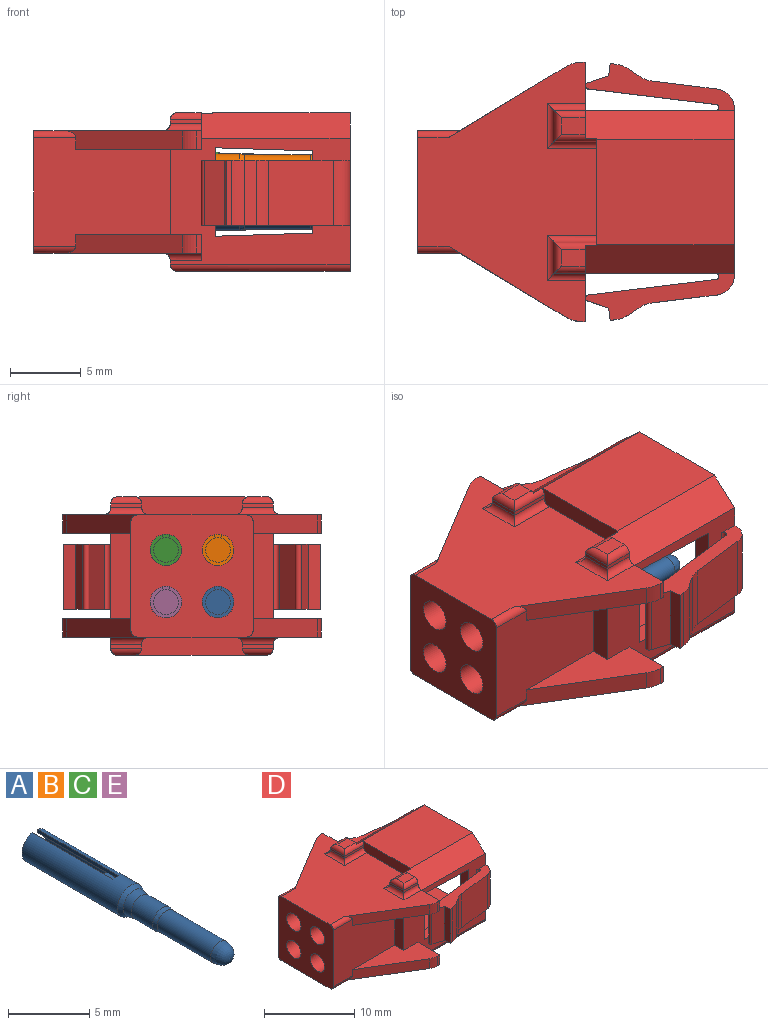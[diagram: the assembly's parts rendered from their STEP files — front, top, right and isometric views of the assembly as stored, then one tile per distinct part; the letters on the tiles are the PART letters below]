
ASSEMBLY  parts=5 mates=4
PART A: 14 faces, bbox 2.2x17x2.2 mm
  f0: cylinder r=0.88mm len=6mm, axis (0,-1,0), area 29.9mm2, adj f8,f9,f10,f12
  f1: cylinder r=0.78mm len=4.65mm, axis (0,-1,0), area 22.6mm2, adj f2,f5
  f2: bspline ~1.71x1.71mm, area 1.6mm2, adj f1,f3
  f3: bspline ~1.86x1.71mm, area 9.9mm2, adj f2,f4
  f4: bspline ~1.86x1.86mm, area 3.5mm2, adj f3,f6
  f5: revolved ~1.55x1.55mm, area 4.4mm2, adj f1
  f6: cone r=0.93mm half-angle=32deg, axis (0,1,0), area 2.4mm2, adj f4,f7
  f7: cylinder r=1.12mm len=8.29mm, axis (0,-1,0), area 55mm2, adj f6,f8,f10,f12,f13
  f8: plane 2.25x2.22mm, normal (0,1,0), area 1.4mm2, adj f0,f7,f10,f12
  f9: plane 1.75x1.75mm, normal (0,1,0), area 2.4mm2, adj f0,f11
  f10: plane 7x0.26mm, normal (-1,0,0), area 1.8mm2, adj f0,f7,f8,f11,f13
  f11: cylinder r=0.88mm len=1mm, axis (0,1,0), area 0.5mm2, adj f9,f10,f12,f13
  f12: plane 7x0.26mm, normal (1,0,0), area 1.8mm2, adj f0,f7,f8,f11,f13
  f13: plane 0.5x0.29mm, normal (0,1,0), area 0.1mm2, adj f7,f10,f11,f12
PART B: same geometry as A
PART C: same geometry as A
PART D: 128 faces, bbox 22.3x18.3x11.2 mm
  f0: plane 2.19x0.28mm, normal (0,1,0), area 0.6mm2, adj f16,f40,f83,f86
  f1: plane 2.19x0.28mm, normal (0,-1,0), area 0.6mm2, adj f11,f49,f88,f91
  f2: plane 11.48x11.2mm, normal (1,0,0), area 43.5mm2, adj f4,f6,f7,f8,f9,f22,f27,f28
  f3: plane 1.69x1.19mm, normal (0,0,1), area 2mm2, adj f49,f91,f92,f93
  f4: plane 9.7x7.44mm, normal (0,0,1), area 72.1mm2, adj f2,f5,f98,f99
  f5: plane 7.59x1.28mm, normal (-1,0,0), area 9.1mm2, adj f4,f24,f60,f61,f82,f85,f90,f93
  f6: plane 13.2x8.88mm, normal (0,1,0), area 60.8mm2, adj f2,f10,f13,f25,f31,f40,f41,f55
  f7: plane 12.7x8.88mm, normal (0,-1,0), area 59.7mm2, adj f2,f14,f15,f31,f45,f49,f50,f51
  f8: plane 9.53x8.2mm, normal (0,-1,0), area 36.5mm2, adj f2,f27,f28,f31,f68,f69,f70
  f9: plane 9.53x8.2mm, normal (0,1,0), area 36.5mm2, adj f2,f27,f30,f31,f65,f66,f67
  f10: plane 2.19x0.28mm, normal (-1,0,0), area 0.6mm2, adj f6,f62,f73,f75
  f11: plane 2.19x0.28mm, normal (-1,0,0), area 0.6mm2, adj f1,f61,f89,f92
  f12: plane 9.64x7.64mm, normal (0,1,0), area 62.8mm2, adj f13,f26,f41,f44,f56,f57,f95,f96
  f13: plane 6.01x1.42mm, normal (-1,0,0), area 8.5mm2, adj f6,f12,f41,f56
  f14: plane 6.01x1.42mm, normal (-1,0,0), area 8.5mm2, adj f7,f23,f45,f50
  f15: plane 2.19x0.28mm, normal (-1,0,0), area 0.6mm2, adj f7,f64,f77,f80
  f16: plane 2.19x0.28mm, normal (-1,0,0), area 0.6mm2, adj f0,f60,f84,f87
  f17: cylinder r=1.12mm len=12.39mm, axis (1,0,0), area 87mm2, adj f26,f39
  f18: cylinder r=1.12mm len=12.39mm, axis (1,0,0), area 87mm2, adj f26,f37
  f19: cylinder r=1.12mm len=12.39mm, axis (1,0,0), area 87mm2, adj f26,f35
  f20: cylinder r=1.12mm len=12.39mm, axis (1,0,0), area 87mm2, adj f26,f33
  f21: plane 1.69x1.19mm, normal (0,0,1), area 2mm2, adj f40,f82,f83,f84
  f22: plane 12.2x10.48mm, normal (0,0,-1), area 107.6mm2, adj f2,f63,f71,f72,f73,f79,f80,f81
  f23: plane 9.64x7.64mm, normal (0,-1,0), area 62.8mm2, adj f14,f26,f45,f46,f50,f54,f94,f97
  f24: plane 18.27x12.64mm, normal (0,0,1), area 134.2mm2, adj f5,f26,f40,f42,f43,f44,f46,f47
  f25: plane 18.27x12.64mm, normal (0,0,-1), area 135.5mm2, adj f6,f26,f51,f52,f53,f54,f55,f57
  f26: plane 8.64x8.64mm, normal (-1,0,0), area 58.8mm2, adj f12,f17,f18,f19,f20,f23,f24,f25
  f27: plane 9.53x8.92mm, normal (0,0,1), area 84.9mm2, adj f2,f8,f9,f31
  f28: plane 9.53x1.19mm, normal (0,-0.67,-0.74), area 15.2mm2, adj f2,f8,f29,f31
  f29: plane 9.53x6.54mm, normal (0,0,-1), area 62.3mm2, adj f2,f28,f30,f31
  f30: plane 9.53x1.19mm, normal (0,0.67,-0.74), area 15.2mm2, adj f2,f9,f29,f31
  f31: plane 11.48x9.26mm, normal (1,0,0), area 66.6mm2, adj f6,f7,f8,f9,f27,f28,f29,f30
  f32: cylinder r=1.56mm len=3.13mm, axis (1,0,0), area 4.1mm2, adj f31,f33
  f33: plane 3.13x3.13mm, normal (1,0,0), area 3.8mm2, adj f20,f32
  f34: cylinder r=1.56mm len=3.13mm, axis (1,0,0), area 4.1mm2, adj f31,f35
  f35: plane 3.13x3.13mm, normal (1,0,0), area 3.8mm2, adj f19,f34
  f36: cylinder r=1.56mm len=3.13mm, axis (1,0,0), area 4.1mm2, adj f31,f37
  f37: plane 3.13x3.13mm, normal (1,0,0), area 3.8mm2, adj f18,f36
  f38: cylinder r=1.56mm len=3.13mm, axis (1,0,0), area 4.1mm2, adj f31,f39
  f39: plane 3.13x3.13mm, normal (1,0,0), area 3.8mm2, adj f17,f38
  f40: plane 5.34x2.59mm, normal (1,0,0), area 6.3mm2, adj f0,f6,f21,f24,f41,f42,f82,f83
  f41: plane 8.85x4.82mm, normal (0,0,-1), area 20.3mm2, adj f6,f12,f13,f40,f42,f43,f44
  f42: plane 1.31x0.32mm, normal (0,1,0), area 0.4mm2, adj f24,f40,f41,f43
  f43: cylinder r=2mm len=1.31mm, axis (0,0,1), area 1.4mm2, adj f24,f41,f42,f44
  f44: plane 8.32x5.03mm, normal (-0.52,0.86,0), area 11.6mm2, adj f12,f24,f41,f43,f95
  f45: plane 8.85x4.82mm, normal (0,0,-1), area 20.3mm2, adj f7,f14,f23,f46,f47,f48,f49
  f46: plane 8.32x5.03mm, normal (-0.52,-0.86,0), area 11.6mm2, adj f23,f24,f45,f47,f94
  f47: cylinder r=2mm len=1.31mm, axis (0,0,1), area 1.4mm2, adj f24,f45,f46,f48
  f48: plane 1.31x0.32mm, normal (0,-1,0), area 0.4mm2, adj f24,f45,f47,f49
  f49: plane 5.34x2.59mm, normal (1,0,0), area 6.3mm2, adj f1,f3,f7,f24,f45,f48,f88,f91
  f50: plane 8.85x4.82mm, normal (0,0,1), area 20.3mm2, adj f7,f14,f23,f51,f52,f53,f54
  f51: plane 3.4x1.81mm, normal (1,0,0), area 4.5mm2, adj f7,f25,f50,f52,f76
  f52: plane 1.31x0.32mm, normal (0,-1,0), area 0.4mm2, adj f25,f50,f51,f53
  f53: cylinder r=2mm len=1.31mm, axis (0,0,-1), area 1.4mm2, adj f25,f50,f52,f54
  f54: plane 8.32x5.03mm, normal (-0.52,-0.86,0), area 11.6mm2, adj f23,f25,f50,f53,f97
  f55: plane 3.4x1.31mm, normal (1,0,0), area 4.5mm2, adj f6,f25,f56,f59
  f56: plane 8.85x4.82mm, normal (0,0,1), area 20.3mm2, adj f6,f12,f13,f55,f57,f58,f59
  f57: plane 8.32x5.03mm, normal (-0.52,0.86,0), area 11.6mm2, adj f12,f25,f56,f58,f96
  f58: cylinder r=2mm len=1.31mm, axis (0,0,-1), area 1.4mm2, adj f25,f56,f57,f59
  f59: plane 1.31x0.32mm, normal (0,1,0), area 0.4mm2, adj f25,f55,f56,f58
  f60: plane 3x0.28mm, normal (0,-1,0), area 0.8mm2, adj f5,f16,f82,f85
  f61: plane 3x0.28mm, normal (0,1,0), area 0.8mm2, adj f5,f11,f90,f93
  f62: plane 3x0.28mm, normal (0,-1,0), area 0.8mm2, adj f10,f63,f71,f74
  f63: plane 8.1x1.28mm, normal (-1,0,0), area 9.1mm2, adj f22,f25,f62,f64,f71,f74,f78,f81
  f64: plane 3x0.28mm, normal (0,1,0), area 0.8mm2, adj f15,f63,f78,f81
  f65: plane 6.9x1.28mm, normal (-0.03,0,1), area 8.8mm2, adj f7,f9,f31,f66
  f66: plane 5.8x1.28mm, normal (-1,0,0), area 7.4mm2, adj f7,f9,f65,f67
  f67: plane 6.9x1.28mm, normal (-0.03,0,-1), area 8.8mm2, adj f7,f9,f31,f66
  f68: plane 6.9x1.28mm, normal (-0.03,0,-1), area 8.8mm2, adj f6,f8,f31,f69
  f69: plane 5.8x1.28mm, normal (-1,0,0), area 7.4mm2, adj f6,f8,f68,f70
  f70: plane 6.9x1.28mm, normal (-0.03,0,1), area 8.8mm2, adj f6,f8,f31,f69
  f71: cylinder r=0.5mm len=3mm, axis (-1,0,0), area 2.2mm2, adj f22,f62,f63,f73
  f72: cylinder r=0.5mm len=12.7mm, axis (-1,0,0), area 9.8mm2, adj f2,f6,f22,f73
  f73: cylinder r=0.5mm len=2.19mm, axis (0,-1,0), area 1.4mm2, adj f10,f22,f71,f72
  f74: cylinder r=0.5mm len=3.5mm, axis (-1,0,0), area 2.5mm2, adj f25,f62,f63,f75
  f75: cylinder r=0.5mm len=2.69mm, axis (0,1,0), area 1.9mm2, adj f6,f10,f25,f74
  f76: cylinder r=0.5mm len=2.69mm, axis (-1,0,0), area 1.9mm2, adj f7,f25,f51,f77
  f77: cylinder r=0.5mm len=3.19mm, axis (0,1,0), area 2mm2, adj f15,f25,f76,f78
  f78: cylinder r=0.5mm len=3.5mm, axis (1,0,0), area 2.5mm2, adj f25,f63,f64,f77
  f79: cylinder r=0.5mm len=12.7mm, axis (1,0,0), area 9.8mm2, adj f2,f7,f22,f80
  f80: cylinder r=0.5mm len=2.19mm, axis (0,-1,0), area 1.4mm2, adj f15,f22,f79,f81
  f81: cylinder r=0.5mm len=3mm, axis (1,0,0), area 2.2mm2, adj f22,f63,f64,f80
  f82: cylinder r=0.5mm len=3mm, axis (-1,0,0), area 2mm2, adj f5,f21,f40,f60,f84,f99
  f83: cylinder r=0.5mm len=2.19mm, axis (1,0,0), area 1.6mm2, adj f0,f21,f40,f84
  f84: cylinder r=0.5mm len=2.19mm, axis (0,1,0), area 1.4mm2, adj f16,f21,f82,f83
  f85: cylinder r=0.5mm len=3.5mm, axis (1,0,0), area 2.5mm2, adj f5,f24,f60,f87
  f86: cylinder r=0.5mm len=2.69mm, axis (1,0,0), area 1.9mm2, adj f0,f24,f40,f87
  f87: cylinder r=0.5mm len=3.19mm, axis (0,-1,0), area 2mm2, adj f16,f24,f85,f86
  f88: cylinder r=0.5mm len=2.69mm, axis (-1,0,0), area 1.9mm2, adj f1,f24,f49,f89
  f89: cylinder r=0.5mm len=3.19mm, axis (0,-1,0), area 2mm2, adj f11,f24,f88,f90
  f90: cylinder r=0.5mm len=3.5mm, axis (-1,0,0), area 2.5mm2, adj f5,f24,f61,f89
  f91: cylinder r=0.5mm len=2.19mm, axis (-1,0,0), area 1.6mm2, adj f1,f3,f49,f92
  f92: cylinder r=0.5mm len=2.19mm, axis (0,1,0), area 1.4mm2, adj f3,f11,f91,f93
  f93: cylinder r=0.5mm len=3mm, axis (1,0,0), area 2mm2, adj f3,f5,f49,f61,f92,f98
  f94: cylinder r=0.5mm len=2.98mm, axis (-1,0,0), area 2.1mm2, adj f23,f24,f26,f46
  f95: cylinder r=0.5mm len=2.98mm, axis (1,0,0), area 2.1mm2, adj f12,f24,f26,f44
  f96: cylinder r=0.5mm len=2.98mm, axis (-1,0,0), area 2.1mm2, adj f12,f25,f26,f57
  f97: cylinder r=0.5mm len=2.98mm, axis (1,0,0), area 2.1mm2, adj f23,f25,f26,f54
  f98: plane 10.51x2.02mm, normal (0,-0.67,0.74), area 28.5mm2, adj f2,f4,f5,f7,f49,f93
  f99: plane 10.51x2.02mm, normal (0,0.67,0.74), area 28.5mm2, adj f2,f4,f5,f6,f40,f82
  f100: cylinder r=0.22mm len=4.6mm, axis (0,0,-1), area 3.2mm2, adj f101,f108,f109,f110
  f101: plane 4.6x1.44mm, normal (-0.32,-0.95,0), area 7mm2, adj f100,f102,f109,f110
  f102: plane 4.6x0.86mm, normal (-0.99,-0.12,0), area 4mm2, adj f101,f103,f109,f110
  f103: plane 4.6x0.4mm, normal (0.12,-0.99,0), area 1.9mm2, adj f102,f109,f110,f125
  f104: plane 4.6x0.84mm, normal (0.55,-0.83,0), area 4.7mm2, adj f109,f110,f125,f126
  f105: plane 4.6x4.59mm, normal (0.12,-0.99,0), area 21.3mm2, adj f109,f110,f126,f127
  f106: cylinder r=1.36mm len=4.6mm, axis (0,0,-1), area 9.9mm2, adj f2,f109,f110,f127
  f107: cylinder r=0.22mm len=4.6mm, axis (0,0,-1), area 3.2mm2, adj f7,f108,f109,f110
  f108: plane 8.98x4.6mm, normal (-0.12,0.99,0), area 41.6mm2, adj f100,f107,f109,f110
  f109: plane 10.52x3.32mm, normal (0,0,1), area 12.6mm2, adj f7,f100,f101,f102,f103,f104,f105,f106
  f110: plane 10.52x3.32mm, normal (0,0,-1), area 12.6mm2, adj f7,f100,f101,f102,f103,f104,f105,f106
  f111: cylinder r=0.22mm len=4.6mm, axis (0,0,-1), area 3.2mm2, adj f112,f119,f120,f121
  f112: plane 8.98x4.6mm, normal (-0.12,-0.99,0), area 41.6mm2, adj f111,f113,f120,f121
  f113: cylinder r=0.22mm len=4.6mm, axis (0,0,-1), area 3.2mm2, adj f6,f112,f120,f121
  f114: cylinder r=1.36mm len=4.6mm, axis (0,0,-1), area 9.9mm2, adj f2,f120,f121,f122
  f115: plane 4.6x4.59mm, normal (0.12,0.99,0), area 21.3mm2, adj f120,f121,f122,f123
  f116: plane 4.6x0.84mm, normal (0.55,0.83,0), area 4.7mm2, adj f120,f121,f123,f124
  f117: plane 4.6x0.4mm, normal (0.12,0.99,0), area 1.9mm2, adj f118,f120,f121,f124
  f118: plane 4.6x0.86mm, normal (-0.99,0.12,0), area 4mm2, adj f117,f119,f120,f121
  f119: plane 4.6x1.44mm, normal (-0.32,0.95,0), area 7mm2, adj f111,f118,f120,f121
  f120: plane 10.52x3.32mm, normal (0,0,1), area 12.6mm2, adj f6,f111,f112,f113,f114,f115,f116,f117
  f121: plane 10.52x3.32mm, normal (0,0,-1), area 12.6mm2, adj f6,f111,f112,f113,f114,f115,f116,f117
  f122: cylinder r=2mm len=4.6mm, axis (0,0,-1), area 0mm2, adj f114,f115,f120,f121
  f123: cylinder r=2mm len=4.6mm, axis (0,0,1), area 4.2mm2, adj f115,f116,f120,f121
  f124: cylinder r=2mm len=4.6mm, axis (0,0,-1), area 4.2mm2, adj f116,f117,f120,f121
  f125: cylinder r=2mm len=4.6mm, axis (0,0,-1), area 4.2mm2, adj f103,f104,f109,f110
  f126: cylinder r=2mm len=4.6mm, axis (0,0,1), area 4.2mm2, adj f104,f105,f109,f110
  f127: cylinder r=2mm len=4.6mm, axis (0,0,-1), area 0mm2, adj f105,f106,f109,f110
PART E: same geometry as A
PLACE A rot(axis=(0,0,1),90deg) t=(16.61,15.79,12.16)mm
PLACE B rot(axis=(0,0,1),90deg) t=(16.61,15.79,15.84)mm
PLACE C rot(axis=(0,0,1),90deg) t=(17.54,19.47,15.84)mm
PLACE D t=(19.42,-9.07,3.47)mm
PLACE E rot(axis=(0,0,1),90deg) t=(17.03,19.47,12.16)mm
MATE fastened A.f6 <-> D.f19  axis (-1,0,0) through (9.17,15.79,12.16)mm
MATE fastened D.f17 <-> B.f6  axis (1,0,0) through (9.48,15.79,15.84)mm
MATE fastened C.f7 <-> D.f20  axis (-1,0,0) through (9.79,19.47,15.84)mm
MATE fastened E.f6 <-> D.f18  axis (-1,0,0) through (9.59,19.47,12.16)mm
